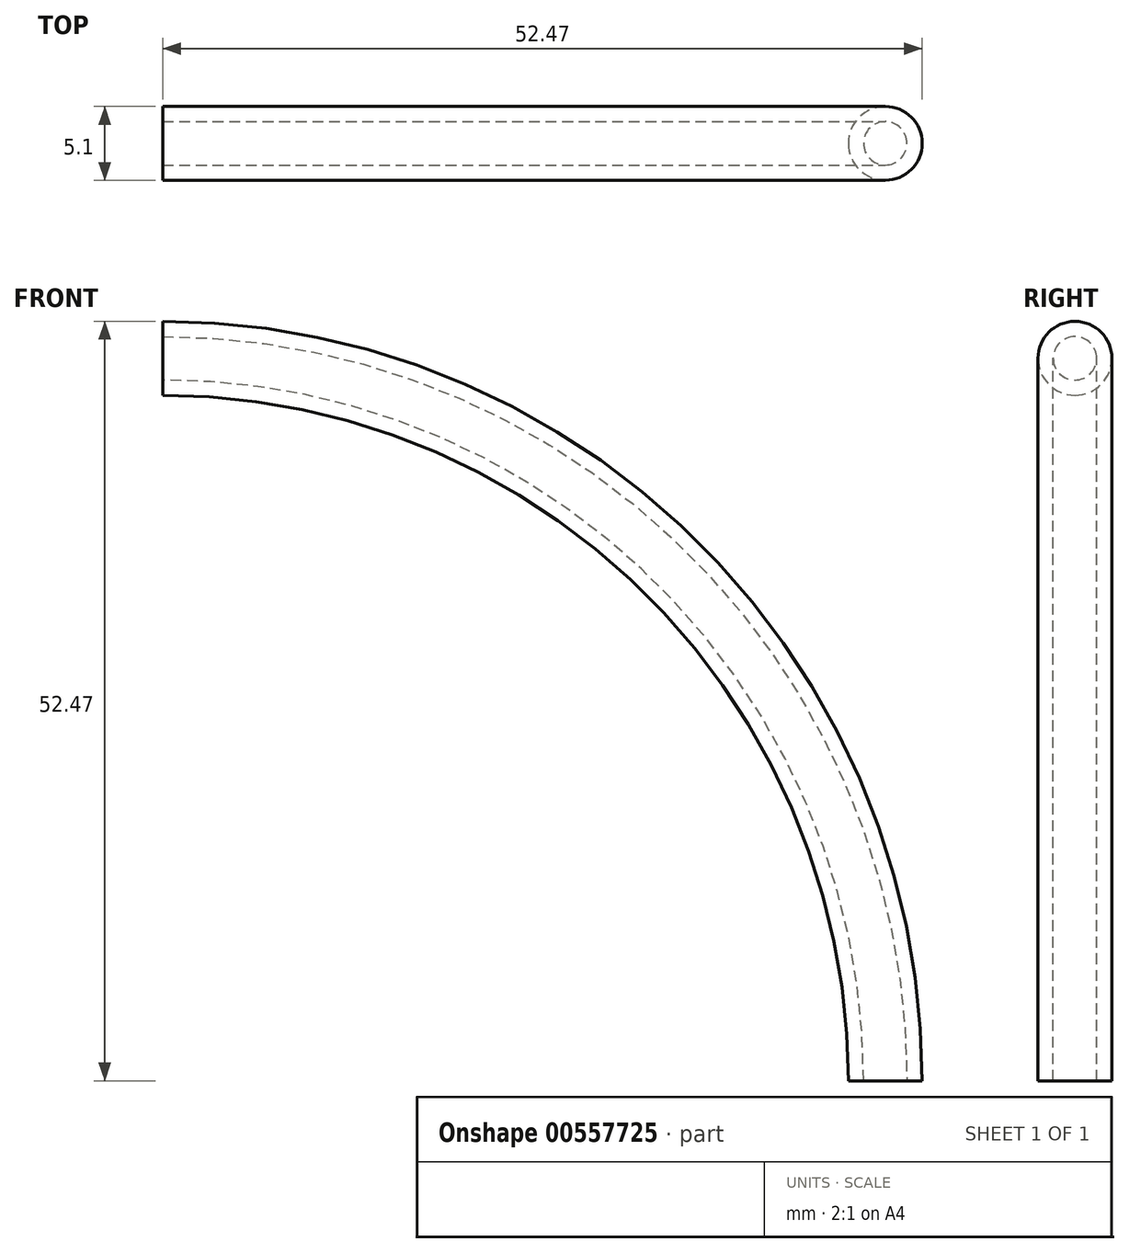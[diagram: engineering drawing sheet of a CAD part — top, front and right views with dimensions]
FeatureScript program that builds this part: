
annotation { "Feature Type Name" : "Feature", "Feature Type Description" : "" }
export const myFeature = defineFeature(function(context is Context, id is Id, definition is map)
    precondition{}
    {
        {
            var Q0;
            Q0=qCreatedBy(makeId("Front.planeOp"),FACE);
            var sketch = newSketch(context, id + "F0", { "sketchPlane" : qUnion([Q0])});
            skLineSegment(sketch, "E0", {"start": v(0, 0) * mm, "end": v(0, 50) * mm, "construction": true});
            skLineSegment(sketch, "E1", {"start": v(0, 0) * mm, "end": v(50, 0) * mm, "construction": true});
            skLineSegment(sketch, "E2", {"start": v(0, 0) * mm, "end": v(20.34, 45.68) * mm, "construction": true});
            skLineSegment(sketch, "E3", {"start": v(0, 0) * mm, "end": v(35.97, 34.73) * mm, "construction": true});
            skLineSegment(sketch, "E4", {"start": v(0, 0) * mm, "end": v(46.36, 18.73) * mm, "construction": true});
            skArc(sketch, "E5", {"start": v(50, 0) * mm, "mid": v(35.36, 35.36) * mm, "end": v(0, 50) * mm});
            skSolve(sketch);
        }
        {
            var Q0;
            Q0=qCreatedBy(makeId("Right.planeOp"),FACE);
            var sketch = newSketch(context, id + "F1", { "sketchPlane" : qUnion([Q0])});
            skCircle(sketch, "E6", {"center": v(-0.03, 49.92) * mm, "radius": 2.55 * mm});
            skSolve(sketch);
        }
        {
            var Q0;
            Q0=makeQuery(id+"F1.imprint","IMPRINT",FACE,{"disambiguationData":[TD([[makeQuery(id+"F1.imprint","IMPRINT",EDGE,{"derivedFrom":sQuery(id+"F1.wireOp",EDGE,"E6")}),1.0]])]});
            var Q1;
            Q1=sQuery(id+"F0.wireOp",EDGE,"E5");
            sweep(context, id + "F2", {"profiles" : qUnion([Q0]), "path" : qUnion([Q1])});
        }
        {
            var Q0;
            Q0=makeQuery(id+"F2.opSweep","CAP_FACE",FACE,{"disambiguationData":[OSD([sQuery(id+"F0.wireOp",VERTEX,"E5.end"),sQuery(id+"F1.wireOp",EDGE,"E6")])],"isStart":true});
            var sketch = newSketch(context, id + "F3", { "sketchPlane" : qUnion([Q0])});
            skCircle(sketch, "E7", {"center": v(0.03, 49.92) * mm, "radius": 1.5 * mm});
            skSolve(sketch);
        }
        {
            var Q0;
            Q0=makeQuery(id+"F3.imprint","IMPRINT",FACE,{"disambiguationData":[TD([[makeQuery(id+"F3.imprint","IMPRINT",EDGE,{"derivedFrom":sQuery(id+"F3.wireOp",EDGE,"E7")}),1.0]])]});
            var Q1;
            Q1=sQuery(id+"F0.wireOp",EDGE,"E5");
            sweep(context, id + "F4", {"operationType" : NewBodyOperationType.REMOVE, "profiles" : qUnion([Q0]), "path" : qUnion([Q1])});
        }
    });
